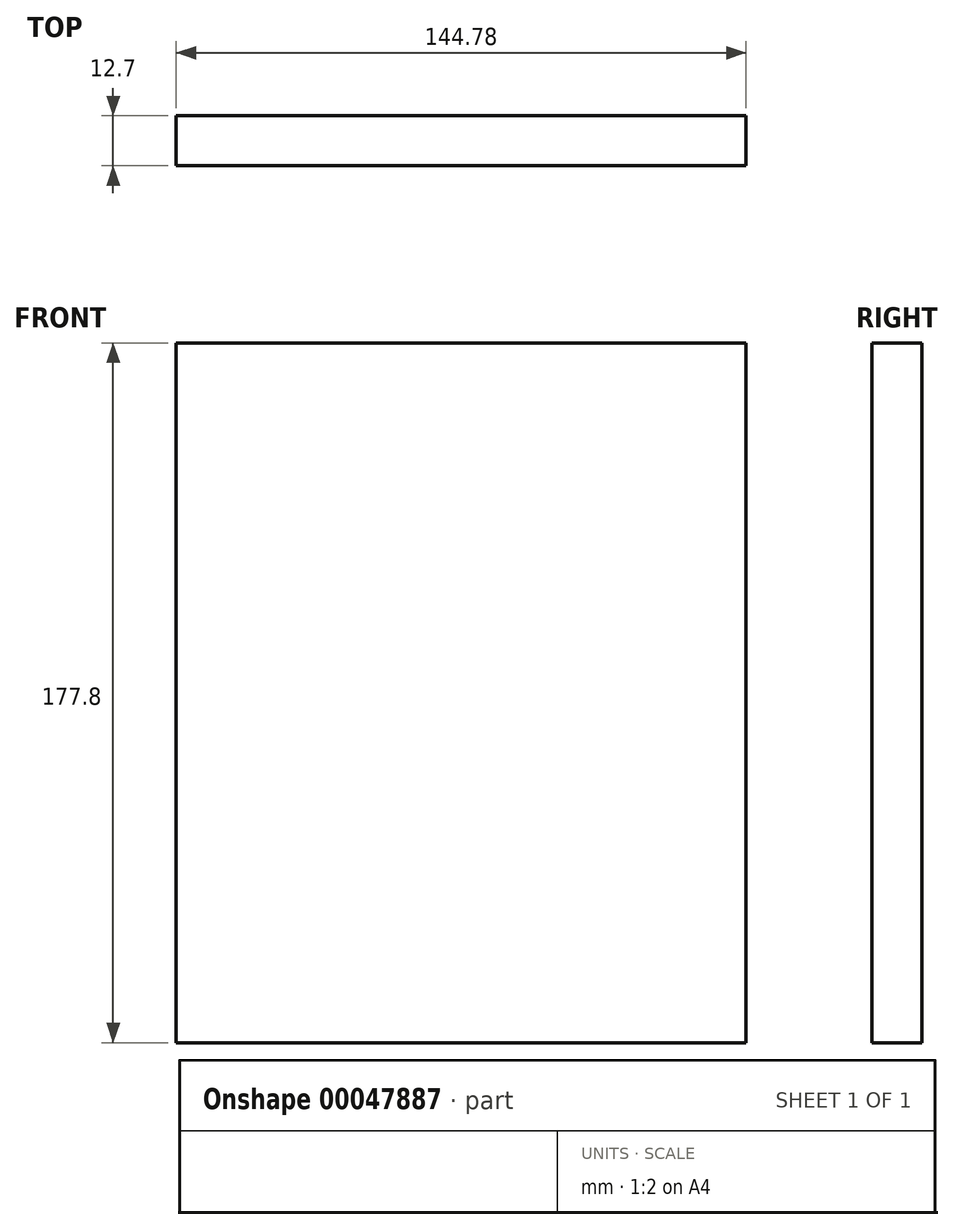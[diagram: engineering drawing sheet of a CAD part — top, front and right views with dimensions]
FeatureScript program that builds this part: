
annotation { "Feature Type Name" : "Feature", "Feature Type Description" : "" }
export const myFeature = defineFeature(function(context is Context, id is Id, definition is map)
    precondition{}
    {
        {
            var Q0;
            Q0=qCreatedBy(makeId("Front.planeOp"),FACE);
            var sketch = newSketch(context, id + "F0", { "sketchPlane" : qUnion([Q0])});
            skLineSegment(sketch, "E0.rect.bottom", {"start": v(72.39, 88.9) * mm, "end": v(-72.4, 88.9) * mm});
            skLineSegment(sketch, "E0.rect.top", {"start": v(72.4, -88.9) * mm, "end": v(-72.39, -88.9) * mm});
            skLineSegment(sketch, "E0.rect.left", {"start": v(72.39, 88.9) * mm, "end": v(72.4, -88.9) * mm});
            skLineSegment(sketch, "E0.rect.right", {"start": v(-72.4, 88.9) * mm, "end": v(-72.39, -88.9) * mm});
            skPoint(sketch, "E0.rect.middle", {"position": v(0, 0) * mm});
            skSolve(sketch);
        }
        {
            var Q0;
            Q0=makeQuery(id+"F0.imprint","IMPRINT",FACE,{"disambiguationData":[TD([[makeQuery(id+"F0.imprint","IMPRINT",EDGE,{"derivedFrom":sQuery(id+"F0.wireOp",EDGE,"E0.rect.bottom")}),1.0]])]});
            extrude(context, id + "F1", {"entities" : qUnion([Q0]), "depth" : 12.7 * mm});
        }
    });
